# Revit family: K8.2 - Freespace
name_source: partatom
category: Communication Devices
revit_build: Autodesk Revit 2017 (Build: 20190508_0315(x64)
units: mm (PartAtom-declared; Revit-internal decimal feet)

## family parameters
Always vertical = No
Cut with Voids When Loaded = No
Maintain Annotation Orientation = No
Part Type = Normal
Room Calculation Point = No
Round Connector Dimension = Use Diameter
Shared = No
Work Plane-Based = Yes

## types (1)
- K8.2 - Freespace
    Coverage Horizontal = 105.00°
    Coverage Vertical = 105.00°
    Default Elevation = 0' - 0"
    Depth = 0' - 10 29/32"
    Description = Multi-purpose, 2-way active loudspeaker
    Height = 1' - 5 11/16"
    Manufacturer = QSC
    Manufacturer URL = qsc.com
    Model = K8.2
    Product Documentation Link = https://www.qsc.com
    Product Page URL = https://www.qsc.com
    Regulatory Compliance = CE, RAEE, UL, China RoHS, RoHS II, FCC Class B
    SPL Max = 128
    Weight Dimensional (kg) = 14.4
    Weight Dimensional (lb) = 31.8
    Weight Product (kg) = 12.2
    Weight Product (lb) = 27
    Width = 0' - 11"

## geometry (parser evidence)
native form markers: Blend x1, Sweep x10
no freeform markers — native parametric forms only
